# Revit family: DOT DOUBLE HEAD RAIL 964_DTM60U9.7_W9.7_N9.7
name_source: partatom
category: Luminarias
units: mm (PartAtom-declared; Revit-internal decimal feet)

## family parameters
Compartido = No
Corte con vacíos al cargar = No
Cota de conector redondo = Diámetro de uso
Origen de luz = Sí
Punto de cálculo de habitación = No
Se basa en plano de trabajo = Sí
Siempre vertical = Sí
Tipo de pieza = Normal

## types (12) — shared parameters
Cambio de temperatura de color de luz atenuada = <Ninguno>
Comentarios de vataje = 90-240V
Elevación por defecto = 1219 mm
Fabricante = BRILLANT
Filtro de color = 16777215
Longitud de símbolo de origen de luz = 3048 mm  [stored 10 ft]
Lámpara = 3030SMD PHILIPS
Watt per fixture = 80
Ángulo de inclinación = 60.00°

## per-type parameters (varying)
| type | Descripción | Modelo | Ángulo de campo de foco | Ángulo de enfoque |
| DOT DOUBLE HEAD RAIL 964_DTM60U9.7.24 | LUMINARIA DE DOBLE CABEZAL TIPO DOWNLIGHT EN FORMATO RECTANGULAR COMPATIBLE CON RIEL DE 6 ENTRADAS Y 3 CIRCUITOS CON CABEZAL PARA PODER DIRIGIR LA LUMINARIA HASTA 90 GRADOS, CUERPO DE ALUMINIO ACABADO EN COLOR NEGRO, IP 20, PESO 4.16Kg, TIPO DE LED 3030SMD PHILIPS CON 80W TOTAL, 6200 LUMENES, 160LM/W, IRC 90, TEMPERATURA EN BLANCO CALIDO 2700K, 50 MIL HORAS DE VIDA PROMEDIO, APERTURA DE 24 GRADOS POR STOCK, ALIMENTADO A 90-240V | DTM60U9.7.24 | 24.00° | 24.00° |
| DOT DOUBLE HEAD RAIL 964_DTM60U9.7.15 | LUMINARIA DE DOBLE CABEZAL TIPO DOWNLIGHT EN FORMATO RECTANGULAR COMPATIBLE CON RIEL DE 6 ENTRADAS Y 3 CIRCUITOS CON CABEZAL PARA PODER DIRIGIR LA LUMINARIA HASTA 90 GRADOS, CUERPO DE ALUMINIO ACABADO EN COLOR NEGRO, IP 20, PESO 4.16Kg, TIPO DE LED 3030SMD PHILIPS CON 80W TOTAL, 6200 LUMENES, 160LM/W, IRC 90, TEMPERATURA EN BLANCO CALIDO 2700K, 50 MIL HORAS DE VIDA PROMEDIO, APERTURA DE 15 GRADOS POR PROYECTO, ALIMENTADO A 90-240V | DTM60U9.7.15 | 15.00° | 15.00° |
| DOT DOUBLE HEAD RAIL 964_DTM60U9.7.36 | LUMINARIA DE DOBLE CABEZAL TIPO DOWNLIGHT EN FORMATO RECTANGULAR COMPATIBLE CON RIEL DE 6 ENTRADAS Y 3 CIRCUITOS CON CABEZAL PARA PODER DIRIGIR LA LUMINARIA HASTA 90 GRADOS, CUERPO DE ALUMINIO ACABADO EN COLOR NEGRO, IP 20, PESO 4.16Kg, TIPO DE LED 3030SMD PHILIPS CON 80W TOTAL, 6200 LUMENES, 160LM/W, IRC 90, TEMPERATURA EN BLANCO CALIDO 2700K, 50 MIL HORAS DE VIDA PROMEDIO, APERTURA DE 36 GRADOS POR PROYECTO, ALIMENTADO A 90-240V | DTM60U9.7.36 | 36.00° | 36.00° |
| DOT DOUBLE HEAD RAIL 964_DTM60U9.7.1535 | LUMINARIA DE DOBLE CABEZAL TIPO DOWNLIGHT EN FORMATO RECTANGULAR COMPATIBLE CON RIEL DE 6 ENTRADAS Y 3 CIRCUITOS CON CABEZAL PARA PODER DIRIGIR LA LUMINARIA HASTA 90 GRADOS, CUERPO DE ALUMINIO ACABADO EN COLOR NEGRO, IP 20, PESO 4.16Kg, TIPO DE LED 3030SMD PHILIPS CON 80W TOTAL, 6200 LUMENES, 160LM/W, IRC 90, TEMPERATURA EN BLANCO CALIDO 2700K, 50 MIL HORAS DE VIDA PROMEDIO, APERTURA ELIPTICA DE 15X35 GRADOS POR PROYECTO, ALIMENTADO A 90-240V | DTM60U9.7.1535 | 15.00° | 35.00° |
| DOT DOUBLE HEAD RAIL 964_DTM60W9.7.24 | LUMINARIA DE DOBLE CABEZAL TIPO DOWNLIGHT EN FORMATO RECTANGULAR COMPATIBLE CON RIEL DE 6 ENTRADAS Y 3 CIRCUITOS CON CABEZAL PARA PODER DIRIGIR LA LUMINARIA HASTA 90 GRADOS, CUERPO DE ALUMINIO ACABADO EN COLOR NEGRO, IP 20, PESO 4.16Kg, TIPO DE LED 3030SMD PHILIPS CON 80W TOTAL, 6300 LUMENES, 162LM/W, IRC 90, TEMPERATURA EN BLANCO CALIDO 3000K, 50 MIL HORAS DE VIDA PROMEDIO, APERTURA DE 24 GRADOS POR STOCK, ALIMENTADO A 90-240V | DTM60W9.7.24 | 24.00° | 24.00° |
| DOT DOUBLE HEAD RAIL 964_DTM60W9.7.15 | LUMINARIA DE DOBLE CABEZAL TIPO DOWNLIGHT EN FORMATO RECTANGULAR COMPATIBLE CON RIEL DE 6 ENTRADAS Y 3 CIRCUITOS CON CABEZAL PARA PODER DIRIGIR LA LUMINARIA HASTA 90 GRADOS, CUERPO DE ALUMINIO ACABADO EN COLOR NEGRO, IP 20, PESO 4.16Kg, TIPO DE LED 3030SMD PHILIPS CON 80W TOTAL, 6300 LUMENES, 162LM/W, IRC 90, TEMPERATURA EN BLANCO CALIDO 3000K, 50 MIL HORAS DE VIDA PROMEDIO, APERTURA DE 15 GRADOS POR PROYECTO, ALIMENTADO A 90-240V | DTM60W9.7.15 | 15.00° | 15.00° |
| DOT DOUBLE HEAD RAIL 964_DTM60W9.7.36 | LUMINARIA DE DOBLE CABEZAL TIPO DOWNLIGHT EN FORMATO RECTANGULAR COMPATIBLE CON RIEL DE 6 ENTRADAS Y 3 CIRCUITOS CON CABEZAL PARA PODER DIRIGIR LA LUMINARIA HASTA 90 GRADOS, CUERPO DE ALUMINIO ACABADO EN COLOR NEGRO, IP 20, PESO 4.16Kg, TIPO DE LED 3030SMD PHILIPS CON 80W TOTAL, 6300 LUMENES, 162LM/W, IRC 90, TEMPERATURA EN BLANCO CALIDO 3000K, 50 MIL HORAS DE VIDA PROMEDIO, APERTURA DE 36 GRADOS POR PROYECTO, ALIMENTADO A 90-240V | DTM60W9.7.36 | 36.00° | 36.00° |
| DOT DOUBLE HEAD RAIL 964_DTM60W9.7.1535 | LUMINARIA DE DOBLE CABEZAL TIPO DOWNLIGHT EN FORMATO RECTANGULAR COMPATIBLE CON RIEL DE 6 ENTRADAS Y 3 CIRCUITOS CON CABEZAL PARA PODER DIRIGIR LA LUMINARIA HASTA 90 GRADOS, CUERPO DE ALUMINIO ACABADO EN COLOR NEGRO, IP 20, PESO 4.16Kg, TIPO DE LED 3030SMD PHILIPS CON 80W TOTAL, 6300 LUMENES, 162LM/W, IRC 90, TEMPERATURA EN BLANCO CALIDO 3000K, 50 MIL HORAS DE VIDA PROMEDIO, APERTURA ELIPTICA DE 15X35 GRADOS POR PROYECTO, ALIMENTADO A 90-240V | DTM60W9.7.1535 | 15.00° | 35.00° |
| DOT DOUBLE HEAD RAIL 964_DTM60N9.7.24 | LUMINARIA DE DOBLE CABEZAL TIPO DOWNLIGHT EN FORMATO RECTANGULAR COMPATIBLE CON RIEL DE 6 ENTRADAS Y 3 CIRCUITOS CON CABEZAL PARA PODER DIRIGIR LA LUMINARIA HASTA 90 GRADOS, CUERPO DE ALUMINIO ACABADO EN COLOR NEGRO, IP 20, PESO 4.16Kg, TIPO DE LED 3030SMD PHILIPS CON 80W TOTAL, 6400 LUMENES, 164LM/W, IRC 90, TEMPERATURA EN BLANCO FRIO 4000K, 50 MIL HORAS DE VIDA PROMEDIO, APERTURA DE 24 GRADOS POR STOCK, ALIMENTADO A 90-240V | DTM60N9.7.24 | 24.00° | 24.00° |
| DOT DOUBLE HEAD RAIL 964_DTM60N9.7.36 | LUMINARIA DE DOBLE CABEZAL TIPO DOWNLIGHT EN FORMATO RECTANGULAR COMPATIBLE CON RIEL DE 6 ENTRADAS Y 3 CIRCUITOS CON CABEZAL PARA PODER DIRIGIR LA LUMINARIA HASTA 90 GRADOS, CUERPO DE ALUMINIO ACABADO EN COLOR NEGRO, IP 20, PESO 4.16Kg, TIPO DE LED 3030SMD PHILIPS CON 80W TOTAL, 6400 LUMENES, 164LM/W, IRC 90, TEMPERATURA EN BLANCO FRIO 4000K, 50 MIL HORAS DE VIDA PROMEDIO, APERTURA DE 36 GRADOS POR PROYECTO, ALIMENTADO A 90-240V | DTM60N9.7.36 | 36.00° | 36.00° |
| DOT DOUBLE HEAD RAIL 964_DTM60N9.7.15 | LUMINARIA DE DOBLE CABEZAL TIPO DOWNLIGHT EN FORMATO RECTANGULAR COMPATIBLE CON RIEL DE 6 ENTRADAS Y 3 CIRCUITOS CON CABEZAL PARA PODER DIRIGIR LA LUMINARIA HASTA 90 GRADOS, CUERPO DE ALUMINIO ACABADO EN COLOR NEGRO, IP 20, PESO 4.16Kg, TIPO DE LED 3030SMD PHILIPS CON 80W TOTAL, 6400 LUMENES, 164LM/W, IRC 90, TEMPERATURA EN BLANCO FRIO 4000K, 50 MIL HORAS DE VIDA PROMEDIO, APERTURA DE 15 GRADOS POR PROYECTO, ALIMENTADO A 90-240V | DTM60N9.7.15 | 15.00° | 15.00° |
| DOT DOUBLE HEAD RAIL 964_DTM60N9.7.1535 | LUMINARIA DE DOBLE CABEZAL TIPO DOWNLIGHT EN FORMATO RECTANGULAR COMPATIBLE CON RIEL DE 6 ENTRADAS Y 3 CIRCUITOS CON CABEZAL PARA PODER DIRIGIR LA LUMINARIA HASTA 90 GRADOS, CUERPO DE ALUMINIO ACABADO EN COLOR NEGRO, IP 20, PESO 4.16Kg, TIPO DE LED 3030SMD PHILIPS CON 80W TOTAL, 6400 LUMENES, 164LM/W, IRC 90, TEMPERATURA EN BLANCO FRIO 4000K, 50 MIL HORAS DE VIDA PROMEDIO, APERTURA ELIPTICA DE 15X35 GRADOS POR PROYECTO, ALIMENTADO A 90-240V | DTM60N9.7.1535 | 15.00° | 35.00° |

note: [stored X ft] marks values corroborated as IEEE doubles in the binary element streams (Revit-internal decimal feet)

## geometry (parser evidence)
native form markers: Blend x2
no freeform markers — native parametric forms only
